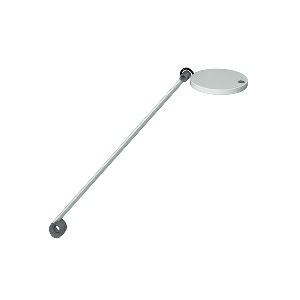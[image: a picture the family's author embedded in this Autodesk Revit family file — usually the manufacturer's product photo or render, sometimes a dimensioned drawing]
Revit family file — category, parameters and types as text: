
# Revit family: para_mi_-_mftl_102_r__930_00643780_b0ea
name_source: partatom
category: Lighting Fixtures
units: mm (PartAtom-declared; Revit-internal decimal feet)

## family parameters
Cut with Voids When Loaded = No
Host = Face
Light Source = No
Part Type = Normal
Room Calculation Point = No
Round Connector Dimension = Use Diameter
Shared = No

## types (1)
- PARA.MI - MFTL 102 R /930 (1 x LED, 580 lm, 3000K)
    Apparent Load = 7 VA
    Approval mark = CE
    CIE Flux Codes = 69 94 99 100 100
    Color Rendering = 90-100
    Color Temperature = 3000K
    Control Gear = Electronic ballast
    Default Elevation = 1800 mm
    Description = MFTL 102 R|Task luminaire|light source: LED|work equipment: Electronic plug-in transformer|connected load: 100-240 V, 50/60 Hz|Power consumption: approx. 7 W|luminous flux: 580 lm|luminous efficacy: 82 lm/W|Illuminance efficiency factor: 107 lx/W|colour temperature: Warm white, ca. 3000 K|color rendering index (CRI): >= 90|chromaticity tolerance:  3 SDCM|class of protection: II with plug-in power supply, III without plug-in power supply|technology: Continuously dimmable|luminaire body|material: Aluminium|surface: Painted|colour: Silver|lamp cover: Plastic, Clear|tubular sections|material: Tubular aluminium section|surface: Painted|colour: Silver metallic|weight (net): approx. 1.0 kg|mains lead: 3.00 m Mains plug BS 1363, CEE 7/XVI, NEMA 1-15P|Fastening: Adaptor (accessory), Table base (accessory), Table clamp (accessory), Tap16|glare control: Reflector|special features: Automatic switchoff adjustable, Push button in luminaire head, Behaviour at net recovery adjustable|Approval mark: C - ETL - US (F. CAN U. USA), VDE - ENEC SEP LIGHT & POWER SUPPLY UNIT|
    Height = 12 mm  [stored 0.0393701 ft]
    Lamp = 1 x LED
    Lamp Light Flux = 580 lm
    Lamp count = 1
    Length = 123 mm
    Luminous efficacy = 83 lm/W
    Manufacturer = Waldmann
    ModVariant = No
    Model = 00643780
    Mounting Place = Table
    Mounting Type = Surface mounted
    Number of Poles = 1
    OnlyDefault = Yes
    Power Factor = 1
    Product Name = PARA.MI - MFTL 102 R /930
    Product group = Task luminaire (office)
    ProductGroupID = 21
    Protection Class = Protection class II
    Protection Degree = IP 40
    RLX_Detail_Level = 1
    RLX_Emergency_Light_Flux = 0 lm
    RLX_Emergency_Type = 0
    RLX_Emergency_Type_DB = No
    RlxData = <blob elided: 58765 chars, md5=879c816d>
    Socket = socket
    Standby Power = 0 W
    System Light Flux = 580 lm
    System Power = 7 W
    Type Comments = Product without accessories
    Type Image = 113150000-00643982.jpg
    URL = http://relux.com
    VarID = ---
    Voltage = 230 V
    Voltage Range = 220-240 V
    Weight = 0.00 kg
    Width = 0 mm  [stored 0 ft]

note: [stored X ft] marks values corroborated as IEEE doubles in the binary element streams (Revit-internal decimal feet)

## geometry (parser evidence)
native form markers: Blend x4, Sweep x13
no freeform markers — native parametric forms only
